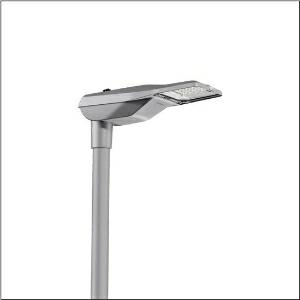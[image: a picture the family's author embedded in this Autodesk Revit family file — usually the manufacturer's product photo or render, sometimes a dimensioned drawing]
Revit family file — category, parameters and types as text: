
# Revit family: streetlight_sl_21_iq_micro___st1_0a_5xe1d31v08db_4967
name_source: partatom
category: Lighting Fixtures
units: mm (PartAtom-declared; Revit-internal decimal feet)

## family parameters
Cut with Voids When Loaded = No
Host = Face
Light Source = No
Part Type = Normal
Room Calculation Point = No
Round Connector Dimension = Use Diameter
Shared = No

## types (1)
- --- (1 x LED, 5110 lm, 39.1 W, 3000K)
    Apparent Load = 39 VA
    CIE Flux Codes = 37 72 97 100 100
    Color Rendering = 70
    Color Temperature = 3000K
    Default Elevation = 1800 mm
    Description = Streetlight SL 21 iQ micro, mast luminaire, primary light control with lens, of PMMA, primary optical cover: cover, of toughened safety glass, transparent, light distribution: ST1.0a, light emission: direct distribution, primary light characteristic: asymmetric, installation type: post-top, side-entry, LED, High Power LED, rated luminous flux: 5.110lm, luminous efficacy: 131lm/W, light colour: 730, colour temperature: 3000K, control gear: iQ-Street Remote, D4i with power reduction, control: pre-setting: logarithmic dimming characteristic, Street-Remote, Auto-Match, Temp-Guard, Lumen-Switch, Night-Set, Smart-Wire, Light-Fading, Desk-Remote (wireless, voltage-free reading and setting of iQ features in the workshop via application-optimized NFC function/RFID function), optimised constant luminous flux control (CLO 2.0), mains connection: 220..240V, AC, 50/60Hz, start of lifetime: 39W, end of service life: 41W, reduction: 17W, luminaire housing, of diecast aluminium, powder-coated, Siteco® metallic grey (DB 702S), corrosivity category C5 mid according to DIN EN ISO 12944, please order mast flange separately, inclination adjustable: 0°, 5°, 10°, 15°, sealing non-destructively replaceable, multi-level sealing system, length: 528mm, width: 235mm, height: 110mm, mast flange for spigot size: 42mm (side-entry): 5XC10008XM4, 60/48mm (side-entry/post-top): 5XC10108XM2, 76/60mm (side-entry/post-top): 5XC10108XM1, mounting height: 4..8m, Smart Interface above, protection rating (complete): IP66, insulation class (complete): insulation class II (safety insulation), certification: CE, ENEC, ENEC+, VDE, impact resistance: IK10, permissible operating ambient temperature for outdoor applications: -40..+50°C, standard-compliant lighting for roads and squares, packaging unit: 1 piece

Light Distribution: ST1.0a
    Height = 110 mm
    Lamp = 1 x LED
    Lamp Light Flux = 5110 lm
    Lamp Power = 39.1 W
    Lamp count = 1
    Length = 528 mm
    Luminous efficacy = 131 lm/W
    Manufacturer = Siteco
    ModVariant = No
    Model = 5XE1D31V08DB
    Number of Poles = 1
    OnlyDefault = Yes
    Power Factor = 1
    Product Name = Streetlight SL 21 iQ micro | ST1.0a
    Product group = mast luminaire | pylon top
    ProductGroupID = 6100
    Protection Class = Protection class II
    Protection Degree = IP 66
    RLX_Detail_Level = 1
    RLX_Emergency_Light_Flux = 0 lm
    RLX_Emergency_Type = 0
    RLX_Emergency_Type_DB = No
    RlxData = <blob elided: 98341 chars, md5=aec803c1>
    Socket = socket
    Standby Power = 0 W
    System Light Flux = 5110 lm
    System Power = 39 W
    Type Comments = factory setting: luminous flux: 100 % | dim-lin: 254 | 765 mA
    Type Image = l_1277292.jpg
    URL = http://relux.com
    VarID = @adj_137123
    Voltage = 0 V
    Weight = 0.00 kg
    Width = 235 mm

## geometry (parser evidence)
native form markers: Blend x4, Sweep x11
no freeform markers — native parametric forms only
